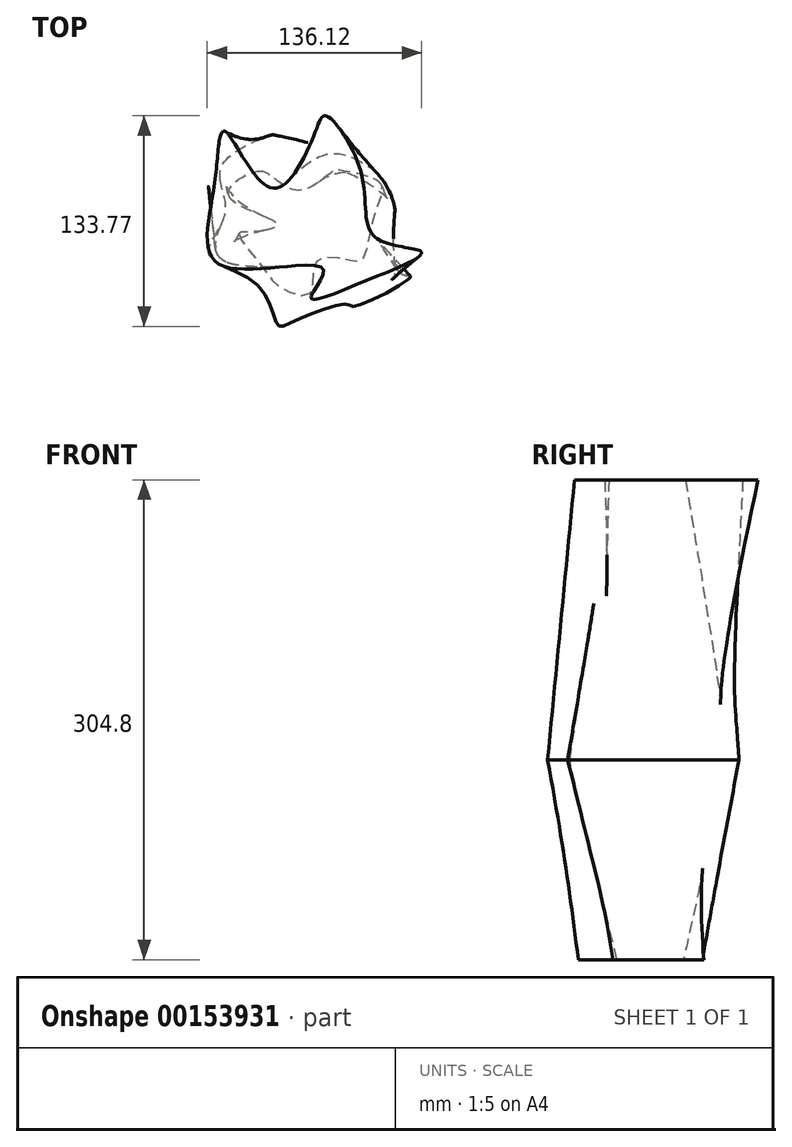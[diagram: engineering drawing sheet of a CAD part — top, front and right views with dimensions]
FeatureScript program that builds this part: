
annotation { "Feature Type Name" : "Feature", "Feature Type Description" : "" }
export const myFeature = defineFeature(function(context is Context, id is Id, definition is map)
    precondition{}
    {
        {
            var Q0;
            Q0=qCreatedBy(makeId("Top.planeOp"),FACE);
            var sketch = newSketch(context, id + "F0", { "sketchPlane" : qUnion([Q0])});
            skFitSpline(sketch, "E0", {"points": [v(-38.39, -25.36) * mm, v(-27.62, -37.9) * mm, v(-8.42, -42.01) * mm, v(-4.11, -21.45) * mm, v(16.84, -20.86) * mm, v(25.46, -19.88) * mm, v(32.7, 8.13) * mm, v(36.63, 27.52) * mm, v(13.9, 35.55) * mm, v(5.88, 35.16) * mm, v(-14.3, 23.4) * mm, v(-32.7, 32.22) * mm, v(-43.09, 34.96) * mm, v(-60.33, 20.47) * mm, v(-30.16, 3.04) * mm, v(-30.95, 0) * mm, v(-46.42, -3.04) * mm, v(-53.47, -4.4) * mm, v(-38.39, -25.36) * mm]});
            skSolve(sketch);
        }
        {
            var Q0;
            Q0=makeQuery(id+"F0.imprint","IMPRINT",FACE,{"disambiguationData":[TD([[makeQuery(id+"F0.imprint","IMPRINT",EDGE,{"derivedFrom":sQuery(id+"F0.wireOp",EDGE,"E0")}),1.0]])]});
            cPlane(context, id + "F1", {"entities" : qUnion([Q0]), "cplaneType" : CPlaneType.OFFSET, "offset" : 127 * mm, "width" : 152.4 * mm, "height" : 152.4 * mm});
        }
        {
            var Q0;
            Q0=qCreatedBy(id+"F1.planeOp",FACE);
            var sketch = newSketch(context, id + "F2", { "sketchPlane" : qUnion([Q0])});
            skFitSpline(sketch, "E1", {"points": [v(-34.08, 58.27) * mm, v(-29.77, 58.27) * mm, v(29.97, 37.7) * mm, v(44.66, 15.38) * mm, v(45.44, 10.28) * mm, v(48.38, -28.7) * mm, v(55.63, -31.63) * mm, v(19.98, -50.24) * mm, v(14.89, -48.87) * mm, v(-20.76, -60.62) * mm, v(-28.8, -62.19) * mm, v(-41.33, -37.12) * mm, v(-72.47, -17.33) * mm, v(-62.09, 9.7) * mm, v(-64.44, 38.88) * mm, v(-34.08, 58.27) * mm]});
            skSolve(sketch);
        }
        {
            var Q0;
            Q0=makeQuery(id+"F2.imprint","IMPRINT",FACE,{"disambiguationData":[TD([[makeQuery(id+"F2.imprint","IMPRINT",EDGE,{"derivedFrom":sQuery(id+"F2.wireOp",EDGE,"E1")}),-1.0]])]});
            var Q1;
            Q1=makeQuery(id+"F0.imprint","IMPRINT",FACE,{"disambiguationData":[TD([[makeQuery(id+"F0.imprint","IMPRINT",EDGE,{"derivedFrom":sQuery(id+"F0.wireOp",EDGE,"E0")}),1.0]])]});
            loft(context, id + "F3", {"sheetProfilesArray" : [{ "sheetProfileEntities" : qUnion([Q0]) }, { "sheetProfileEntities" : qUnion([Q1]) }]});
        }
        {
            var Q0;
            Q0=qCreatedBy(id+"F1.planeOp",FACE);
            cPlane(context, id + "F4", {"entities" : qUnion([Q0]), "cplaneType" : CPlaneType.OFFSET, "offset" : 177.8 * mm, "width" : 152.4 * mm, "height" : 152.4 * mm});
        }
        {
            var Q0;
            Q0=qCreatedBy(id+"F4.planeOp",FACE);
            var sketch = newSketch(context, id + "F5", { "sketchPlane" : qUnion([Q0])});
            skFitSpline(sketch, "E2", {"points": [v(-68.94, 28.1) * mm, v(-62.28, 60.82) * mm, v(-32.51, 24.78) * mm, v(-4.5, 62) * mm, v(1.96, 70.6) * mm, v(24.68, 32.02) * mm, v(33.69, -6.95) * mm, v(62.28, -15.77) * mm, v(23.5, -35.55) * mm, v(-7.83, -44.36) * mm, v(0, -26.54) * mm, v(-64.83, -24.19) * mm, v(-68.94, 28.1) * mm]});
            skSolve(sketch);
        }
        {
            var Q1;
            Q1=makeQuery(id+"F5.imprint","IMPRINT",FACE,{"disambiguationData":[TD([[makeQuery(id+"F5.imprint","IMPRINT",EDGE,{"derivedFrom":sQuery(id+"F5.wireOp",EDGE,"E2")}),-1.0]])]});
            var Q2;
            Q2=makeQuery(id+"F3.opLoft","CAP_FACE",FACE,{"disambiguationData":[OSD([makeQuery(id+"F2.imprint","IMPRINT",FACE,{"disambiguationData":[TD([[makeQuery(id+"F2.imprint","IMPRINT",EDGE,{"derivedFrom":sQuery(id+"F2.wireOp",EDGE,"E1")}),-1.0]])]})])],"isStart":true});
            loft(context, id + "F6", {"operationType" : NewBodyOperationType.ADD, "sheetProfilesArray" : [{ "sheetProfileEntities" : qUnion([Q1]) }, { "sheetProfileEntities" : qUnion([Q2]) }]});
        }
    });
